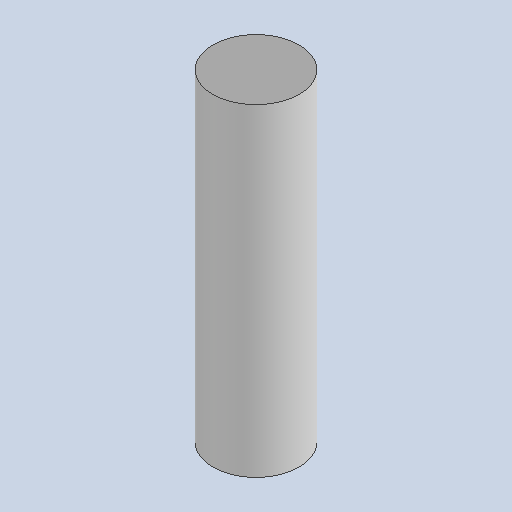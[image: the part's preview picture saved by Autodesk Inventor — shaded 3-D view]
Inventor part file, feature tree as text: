
AUTODESK INVENTOR PART (.ipt)
format: ipt  version: 2025 (Build 290162010, 162A)  size: 131,072 bytes
history: native  units: mm
features: extrude x1, sketch x1
ambient origin geometry x8: Origin, YZ Plane, XZ Plane, XY Plane, X Axis, Y Axis, Z Axis, Center Point
bodies: Solid1 (feature_tree)
feature tree (2):
  extrude  "Extrusion1"  Depth=45.0mm TaperAngle=0.0deg
  sketch  "Sketch1"  dims[d0=12.0mm d1=45.0mm d2=40.0mm d3=0.0mm d4=0.0mm]
